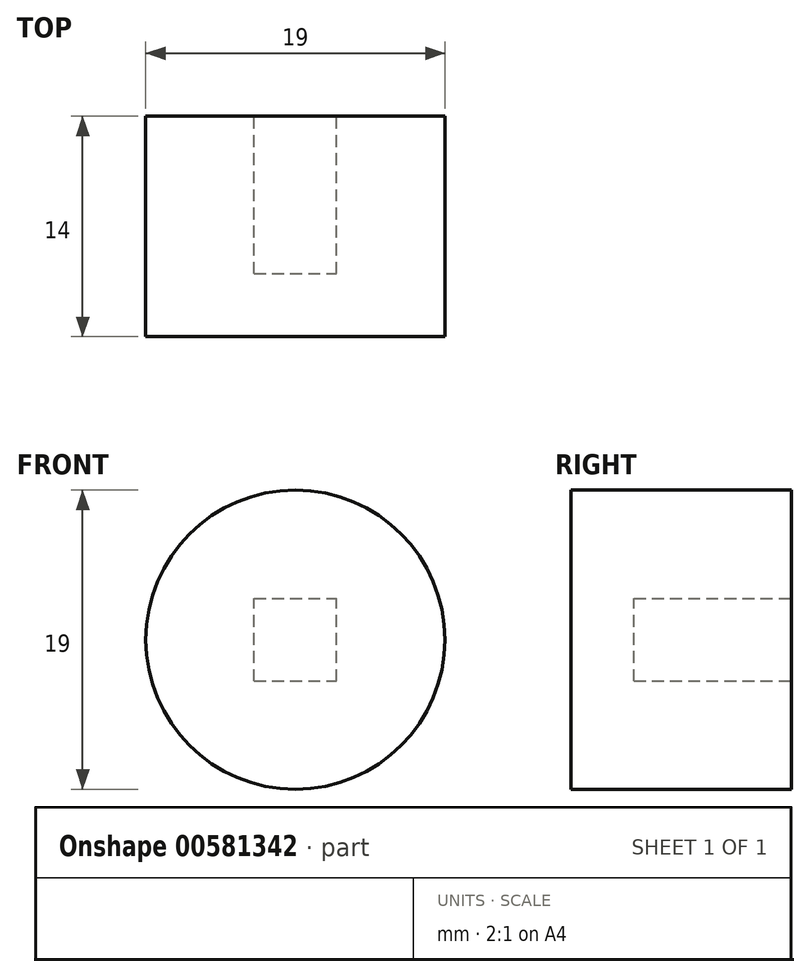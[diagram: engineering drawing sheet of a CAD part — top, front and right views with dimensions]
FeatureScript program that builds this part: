
annotation { "Feature Type Name" : "Feature", "Feature Type Description" : "" }
export const myFeature = defineFeature(function(context is Context, id is Id, definition is map)
    precondition{}
    {
        {
            var Q0;
            Q0=qCreatedBy(makeId("Front.planeOp"),FACE);
            var sketch = newSketch(context, id + "F0", { "sketchPlane" : qUnion([Q0])});
            skCircle(sketch, "E0", {"center": v(0, 0) * mm, "radius": 9.5 * mm});
            skSolve(sketch);
        }
        {
            var Q0;
            Q0=makeQuery(id+"F0.imprint","IMPRINT",FACE,{"disambiguationData":[TD([[makeQuery(id+"F0.imprint","IMPRINT",EDGE,{"derivedFrom":sQuery(id+"F0.wireOp",EDGE,"E0")}),1.0]])]});
            extrude(context, id + "F1", {"entities" : qUnion([Q0]), "depth" : 14 * mm, "offsetDistance" : 25 * mm});
        }
        {
            var Q0;
            Q0=makeQuery(id+"F1.opExtrude","CAP_FACE",FACE,{"disambiguationData":[OSD([sQuery(id+"F0.wireOp",EDGE,"E0")])],"isStart":true});
            var sketch = newSketch(context, id + "F2", { "sketchPlane" : qUnion([Q0])});
            skLineSegment(sketch, "E1.bottom", {"start": v(2.63, -2.62) * mm, "end": v(-2.62, -2.63) * mm});
            skLineSegment(sketch, "E1.top", {"start": v(2.62, 2.63) * mm, "end": v(-2.63, 2.62) * mm});
            skLineSegment(sketch, "E1.left", {"start": v(2.63, -2.62) * mm, "end": v(2.62, 2.63) * mm});
            skLineSegment(sketch, "E1.right", {"start": v(-2.62, -2.63) * mm, "end": v(-2.62, 2.63) * mm});
            skPoint(sketch, "E1.middle", {"position": v(0, 0) * mm});
            skSolve(sketch);
        }
        {
            var Q0;
            Q0=makeQuery(id+"F2.imprint","IMPRINT",FACE,{"disambiguationData":[TD([[makeQuery(id+"F2.imprint","IMPRINT",EDGE,{"derivedFrom":sQuery(id+"F2.wireOp",EDGE,"E1.bottom")}),-1.0]])]});
            extrude(context, id + "F3", {"entities" : qUnion([Q0]), "operationType" : NewBodyOperationType.REMOVE, "oppositeDirection" : true, "depth" : 10 * mm, "offsetDistance" : 25 * mm});
        }
    });
